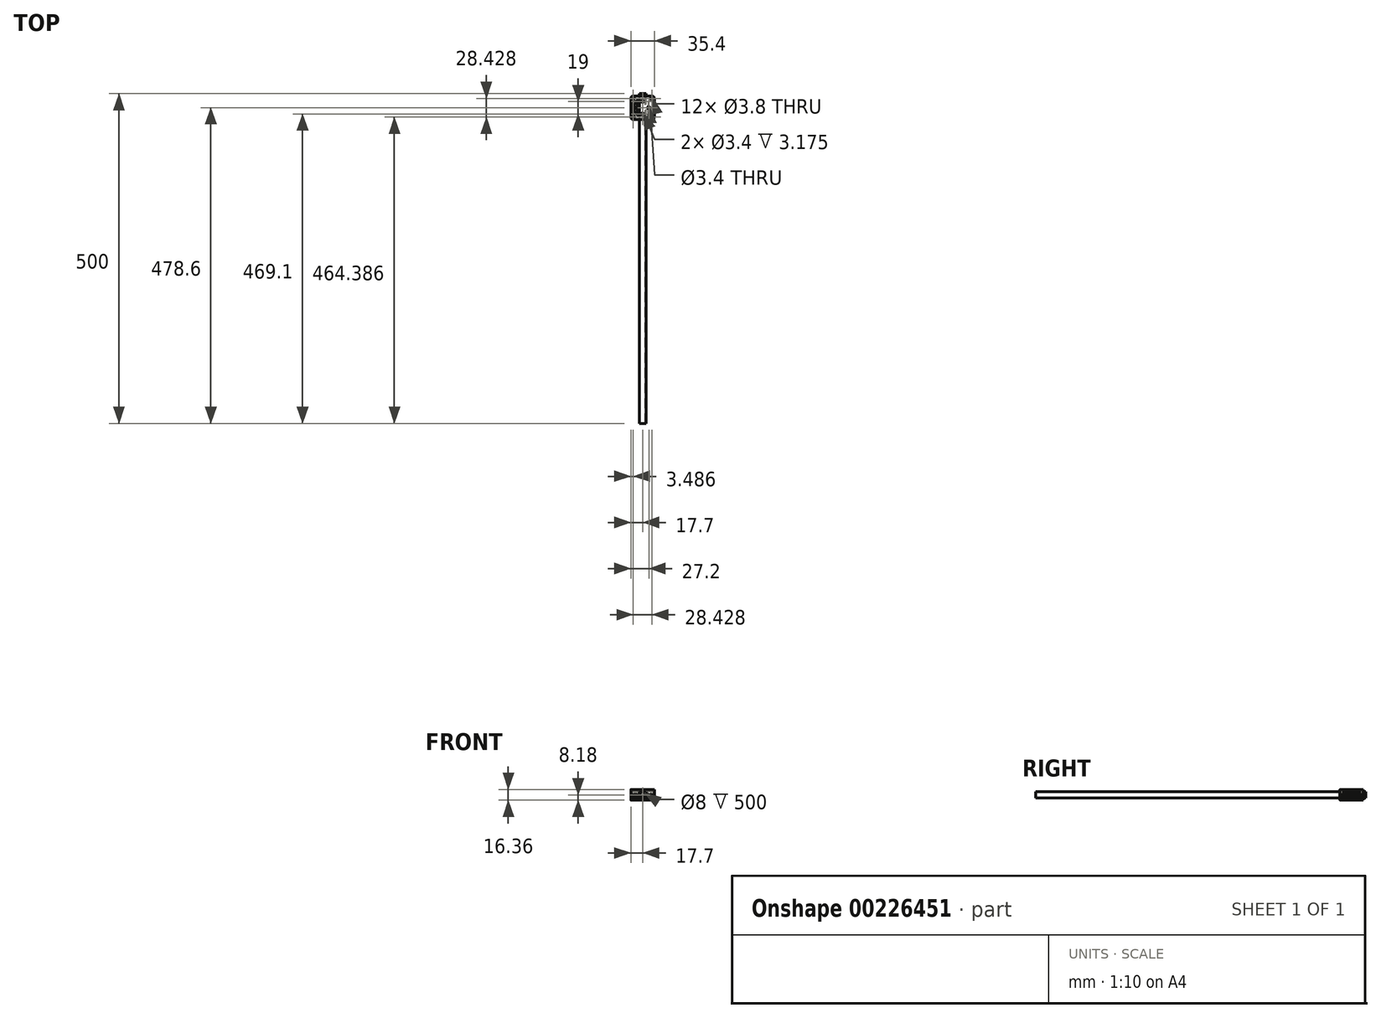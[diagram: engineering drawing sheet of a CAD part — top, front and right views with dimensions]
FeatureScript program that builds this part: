
annotation { "Feature Type Name" : "Feature", "Feature Type Description" : "" }
export const myFeature = defineFeature(function(context is Context, id is Id, definition is map)
    precondition{}
    {
        {
            var Q0;
            Q0=qCreatedBy(makeId("Front.planeOp"),FACE);
            var sketch = newSketch(context, id + "F0", { "sketchPlane" : qUnion([Q0])});
            skLineSegment(sketch, "E0.bottom", {"start": v(-5, 5) * mm, "end": v(5, 5) * mm});
            skLineSegment(sketch, "E0.top", {"start": v(-5, -5) * mm, "end": v(5, -5) * mm});
            skLineSegment(sketch, "E0.left", {"start": v(-5, 5) * mm, "end": v(-5, -5) * mm});
            skLineSegment(sketch, "E0.right", {"start": v(5, 5) * mm, "end": v(5, -5) * mm});
            skPoint(sketch, "E0.middle", {"position": v(0, 0) * mm});
            skCircle(sketch, "E1", {"center": v(0, 0) * mm, "radius": 4 * mm});
            skSolve(sketch);
        }
        {
            var Q0;
            Q0 = qSketchRegion(id + "F0", true);
            extrude(context, id + "F1", {"entities" : qUnion([Q0]), "depth" : 500 * mm, "offsetDistance" : 25.4 * mm, "symmetric" : true});
        }
        {
            var Q0;
            Q0=makeQuery(id+"F1.opExtrude","SWEPT_FACE",FACE,{"disambiguationData":[OSD([sQuery(id+"F0.wireOp",EDGE,"E0.bottom")])]});
            var sketch = newSketch(context, id + "F2", { "sketchPlane" : qUnion([Q0])});
            skCircle(sketch, "E2", {"center": v(0, 228.6) * mm, "radius": 13.5 * mm});
            skCircle(sketch, "E3", {"center": v(0, 228.6) * mm, "radius": 16.67 * mm});
            skLineSegment(sketch, "E4.bottom", {"start": v(-14.52, 246.3) * mm, "end": v(14.52, 246.3) * mm});
            skLineSegment(sketch, "E4.top", {"start": v(-14.52, 210.9) * mm, "end": v(14.52, 210.9) * mm});
            skLineSegment(sketch, "E4.left", {"start": v(-17.7, 243.12) * mm, "end": v(-17.7, 214.08) * mm});
            skLineSegment(sketch, "E4.right", {"start": v(17.7, 243.13) * mm, "end": v(17.7, 214.08) * mm});
            skLineSegment(sketch, "E5", {"start": v(-17.7, 210.9) * mm, "end": v(17.7, 246.3) * mm, "construction": true});
            skCircle(sketch, "E6", {"center": v(-14.21, 214.39) * mm, "radius": 1.9 * mm});
            skLineSegment(sketch, "E7", {"start": v(0, 228.6) * mm, "end": v(0, 246.3) * mm, "construction": true});
            skCircle(sketch, "E8.MirrorC", {"center": v(14.21, 214.39) * mm, "radius": 1.9 * mm});
            skLineSegment(sketch, "E9", {"start": v(0, 228.6) * mm, "end": v(17.7, 228.6) * mm, "construction": true});
            skCircle(sketch, "E10.MirrorC", {"center": v(14.21, 242.81) * mm, "radius": 1.9 * mm});
            skCircle(sketch, "E11.MirrorC", {"center": v(-14.21, 242.81) * mm, "radius": 1.9 * mm});
            skPoint(sketch, "E12.visualSharp", {"position": v(-17.7, 246.3) * mm});
            skArc(sketch, "E12.filletArc", {"start": v(-14.52, 246.3) * mm, "mid": v(-16.77, 245.37) * mm, "end": v(-17.7, 243.12) * mm});
            skPoint(sketch, "E13.visualSharp", {"position": v(17.7, 246.3) * mm});
            skArc(sketch, "E13.filletArc", {"start": v(17.7, 243.13) * mm, "mid": v(16.77, 245.37) * mm, "end": v(14.52, 246.3) * mm});
            skPoint(sketch, "E14.visualSharp", {"position": v(17.7, 210.9) * mm});
            skArc(sketch, "E14.filletArc", {"start": v(14.52, 210.9) * mm, "mid": v(16.77, 211.83) * mm, "end": v(17.7, 214.08) * mm});
            skPoint(sketch, "E15.visualSharp", {"position": v(-17.7, 210.9) * mm});
            skArc(sketch, "E15.filletArc", {"start": v(-17.7, 214.08) * mm, "mid": v(-16.77, 211.83) * mm, "end": v(-14.52, 210.9) * mm});
            skCircle(sketch, "E16", {"center": v(0, 219.1) * mm, "radius": 1.7 * mm});
            skCircle(sketch, "E17.MirrorC", {"center": v(0, 238.1) * mm, "radius": 1.7 * mm});
            skCircle(sketch, "E18.MirrorC", {"center": v(9.5, 228.6) * mm, "radius": 1.7 * mm});
            skCircle(sketch, "E19.MirrorC", {"center": v(-9.5, 228.6) * mm, "radius": 1.7 * mm});
            skSolve(sketch);
        }
        {
            var Q0;
            Q0=makeQuery(id+"F2.imprint","IMPRINT",FACE,{"disambiguationData":[TD([[makeQuery(id+"F2.imprint","IMPRINT",EDGE,{"derivedFrom":sQuery(id+"F2.wireOp",EDGE,"E4.left")}),1.0]])]});
            var Q1;
            {var subQ0=sQuery(id+"F2.wireOp",EDGE,"E3");var subQ1=sQuery(id+"F0.wireOp",EDGE,"E0.bottom");var subQ2=makeQuery(id+"F1.opExtrude","SWEPT_EDGE",EDGE,{"disambiguationData":[OSD([subQ1,sQuery(id+"F0.wireOp",EDGE,"E0.left")])]});var subQ3=makeQuery(id+"F2.imprint","INTERSECT",VERTEX,{"disambiguationData":[OD(0.0)],"derivedFrom":[subQ2,subQ0]});Q1=makeQuery(id+"F2.imprint","IMPRINT",FACE,{"disambiguationData":[TD([[makeQuery(id+"F2.imprint","IMPRINT",EDGE,{"disambiguationData":[TD([[subQ3,1.0]])],"derivedFrom":subQ0}),-1.0]])]});}
            var Q2;
            Q2=makeQuery(id+"F2.imprint","IMPRINT",FACE,{"disambiguationData":[TD([[makeQuery(id+"F2.imprint","IMPRINT",EDGE,{"derivedFrom":sQuery(id+"F2.wireOp",EDGE,"E4.right")}),-1.0]])]});
            var Q3;
            {var subQ0=sQuery(id+"F2.wireOp",EDGE,"E2");var subQ1=makeQuery(id+"F1.opExtrude","SWEPT_EDGE",EDGE,{"disambiguationData":[OSD([sQuery(id+"F0.wireOp",EDGE,"E0.bottom"),sQuery(id+"F0.wireOp",EDGE,"E0.right")])]});var subQ2=makeQuery(id+"F2.imprint","INTERSECT",VERTEX,{"disambiguationData":[OD(0.0)],"derivedFrom":[subQ1,subQ0]});Q3=makeQuery(id+"F2.imprint","IMPRINT",FACE,{"disambiguationData":[TD([[makeQuery(id+"F2.imprint","IMPRINT",EDGE,{"disambiguationData":[TD([[subQ2,1.0]])],"derivedFrom":subQ0}),-1.0]])]});}
            var Q4;
            {var subQ0=sQuery(id+"F2.wireOp",EDGE,"E2");var subQ1=sQuery(id+"F0.wireOp",EDGE,"E0.bottom");var subQ2=makeQuery(id+"F1.opExtrude","SWEPT_EDGE",EDGE,{"disambiguationData":[OSD([subQ1,sQuery(id+"F0.wireOp",EDGE,"E0.left")])]});var subQ3=makeQuery(id+"F2.imprint","INTERSECT",VERTEX,{"disambiguationData":[OD(0.0)],"derivedFrom":[subQ2,subQ0]});Q4=makeQuery(id+"F2.imprint","IMPRINT",FACE,{"disambiguationData":[TD([[makeQuery(id+"F2.imprint","IMPRINT",EDGE,{"disambiguationData":[TD([[subQ3,1.0]])],"derivedFrom":subQ0}),-1.0]])]});}
            var Q5;
            {var subQ0=sQuery(id+"F2.wireOp",EDGE,"E2");var subQ1=makeQuery(id+"F1.opExtrude","SWEPT_EDGE",EDGE,{"disambiguationData":[OSD([sQuery(id+"F0.wireOp",EDGE,"E0.bottom"),sQuery(id+"F0.wireOp",EDGE,"E0.left")])]});var subQ2=makeQuery(id+"F2.imprint","INTERSECT",VERTEX,{"disambiguationData":[OD(0.0)],"derivedFrom":[subQ1,subQ0]});Q5=makeQuery(id+"F2.imprint","IMPRINT",FACE,{"disambiguationData":[TD([[makeQuery(id+"F2.imprint","IMPRINT",EDGE,{"disambiguationData":[TD([[subQ2,-1.0]])],"derivedFrom":subQ0}),-1.0]])]});}
            var Q6;
            Q6=makeQuery(id+"F2.imprint","IMPRINT",FACE,{"disambiguationData":[TD([[makeQuery(id+"F2.imprint","IMPRINT",EDGE,{"derivedFrom":sQuery(id+"F2.wireOp",EDGE,"E19.MirrorC")}),1.0]])]});
            var Q7;
            Q7=makeQuery(id+"F2.imprint","IMPRINT",FACE,{"disambiguationData":[TD([[makeQuery(id+"F2.imprint","IMPRINT",EDGE,{"derivedFrom":sQuery(id+"F2.wireOp",EDGE,"E16")}),-1.0]])]});
            var Q8;
            Q8=makeQuery(id+"F2.imprint","IMPRINT",FACE,{"disambiguationData":[TD([[makeQuery(id+"F2.imprint","IMPRINT",EDGE,{"derivedFrom":sQuery(id+"F2.wireOp",EDGE,"E18.MirrorC")}),-1.0]])]});
            var Q9;
            {var subQ0=sQuery(id+"F2.wireOp",EDGE,"E2");var subQ1=sQuery(id+"F0.wireOp",EDGE,"E0.bottom");var subQ2=makeQuery(id+"F1.opExtrude","SWEPT_EDGE",EDGE,{"disambiguationData":[OSD([subQ1,sQuery(id+"F0.wireOp",EDGE,"E0.left")])]});var subQ3=makeQuery(id+"F2.imprint","INTERSECT",VERTEX,{"disambiguationData":[OD(1.0)],"derivedFrom":[subQ2,subQ0]});Q9=makeQuery(id+"F2.imprint","IMPRINT",FACE,{"disambiguationData":[TD([[makeQuery(id+"F2.imprint","IMPRINT",EDGE,{"disambiguationData":[TD([[subQ3,-1.0]])],"derivedFrom":subQ0}),-1.0]])]});}
            var Q10;
            {var subQ0=sQuery(id+"F2.wireOp",EDGE,"E3");var subQ1=sQuery(id+"F0.wireOp",EDGE,"E0.bottom");var subQ2=makeQuery(id+"F1.opExtrude","SWEPT_EDGE",EDGE,{"disambiguationData":[OSD([subQ1,sQuery(id+"F0.wireOp",EDGE,"E0.left")])]});var subQ3=makeQuery(id+"F2.imprint","INTERSECT",VERTEX,{"disambiguationData":[OD(1.0)],"derivedFrom":[subQ2,subQ0]});Q10=makeQuery(id+"F2.imprint","IMPRINT",FACE,{"disambiguationData":[TD([[makeQuery(id+"F2.imprint","IMPRINT",EDGE,{"disambiguationData":[TD([[subQ3,-1.0]])],"derivedFrom":subQ0}),-1.0]])]});}
            extrude(context, id + "F3", {"entities" : qUnion([Q0, Q1, Q2, Q3, Q4, Q5, Q6, Q7, Q8, Q9, Q10]), "depth" : 3.17 * mm, "offsetDistance" : 25.4 * mm});
        }
        {
            var Q0;
            Q0=makeQuery(id+"F3.opExtrude","CAP_FACE",FACE,{"disambiguationData":[OSD([sQuery(id+"F2.wireOp",EDGE,"E4.bottom"),sQuery(id+"F2.wireOp",EDGE,"E4.top"),sQuery(id+"F2.wireOp",EDGE,"E4.left"),sQuery(id+"F2.wireOp",EDGE,"E4.right"),sQuery(id+"F2.wireOp",EDGE,"E6"),sQuery(id+"F2.wireOp",EDGE,"E8.MirrorC"),sQuery(id+"F2.wireOp",EDGE,"E10.MirrorC"),sQuery(id+"F2.wireOp",EDGE,"E11.MirrorC"),sQuery(id+"F2.wireOp",EDGE,"E12.filletArc"),sQuery(id+"F2.wireOp",EDGE,"E13.filletArc"),sQuery(id+"F2.wireOp",EDGE,"E14.filletArc"),sQuery(id+"F2.wireOp",EDGE,"E15.filletArc"),sQuery(id+"F2.wireOp",EDGE,"E16"),sQuery(id+"F2.wireOp",EDGE,"E17.MirrorC"),sQuery(id+"F2.wireOp",EDGE,"E18.MirrorC"),sQuery(id+"F2.wireOp",EDGE,"E19.MirrorC")])],"isStart":true});
            var sketch = newSketch(context, id + "F4", { "sketchPlane" : qUnion([Q0])});
            skLineSegment(sketch, "E20", {"start": v(-14.52, -217.87) * mm, "end": v(-11.35, -217.87) * mm});
            skLineSegment(sketch, "E21", {"start": v(-8.18, -221.05) * mm, "end": v(-8.18, -225.63) * mm});
            skPoint(sketch, "E22", {"position": v(-9.5, -228.6) * mm});
            skPoint(sketch, "E23.orphan", {"position": v(-8.18, -228.6) * mm});
            skLineSegment(sketch, "E24", {"start": v(-9.5, -228.6) * mm, "end": v(9.5, -228.6) * mm, "construction": true});
            skLineSegment(sketch, "E25.MirrorCS", {"start": v(-8.18, -236.15) * mm, "end": v(-8.18, -231.57) * mm});
            skLineSegment(sketch, "E26.MirrorCS", {"start": v(-14.52, -239.33) * mm, "end": v(-11.35, -239.33) * mm});
            skPoint(sketch, "E27.visualSharp", {"position": v(-8.18, -217.87) * mm});
            skArc(sketch, "E27.filletArc", {"start": v(-8.18, -221.05) * mm, "mid": v(-9.1, -218.8) * mm, "end": v(-11.35, -217.87) * mm});
            skPoint(sketch, "E28.visualSharp", {"position": v(-8.18, -239.33) * mm});
            skArc(sketch, "E28.filletArc", {"start": v(-11.35, -239.33) * mm, "mid": v(-9.1, -238.4) * mm, "end": v(-8.17, -236.15) * mm});
            skLineSegment(sketch, "E29.0", {"start": v(-17.7, -214.7) * mm, "end": v(-17.7, -214.08) * mm});
            skArc(sketch, "E29.1", {"start": v(-17.7, -214.08) * mm, "mid": v(-16.77, -211.83) * mm, "end": v(-14.52, -210.9) * mm});
            skLineSegment(sketch, "E29.2", {"start": v(-14.52, -210.9) * mm, "end": v(14.52, -210.9) * mm});
            skArc(sketch, "E29.3", {"start": v(14.52, -210.9) * mm, "mid": v(16.77, -211.83) * mm, "end": v(17.7, -214.08) * mm});
            skLineSegment(sketch, "E29.4", {"start": v(17.7, -243.13) * mm, "end": v(17.7, -214.08) * mm});
            skLineSegment(sketch, "E29.5", {"start": v(-14.52, -246.3) * mm, "end": v(14.52, -246.3) * mm});
            skArc(sketch, "E29.6", {"start": v(-14.52, -246.3) * mm, "mid": v(-16.77, -245.37) * mm, "end": v(-17.7, -243.12) * mm});
            skArc(sketch, "E29.7", {"start": v(17.7, -243.13) * mm, "mid": v(16.77, -245.37) * mm, "end": v(14.52, -246.3) * mm});
            skLineSegment(sketch, "E30", {"start": v(0, -246.3) * mm, "end": v(0, -210.9) * mm, "construction": true});
            skPoint(sketch, "E31.newPointA", {"position": v(-17.7, -243.12) * mm});
            skPoint(sketch, "E31.newPointB", {"position": v(-17.7, -217.87) * mm});
            skArc(sketch, "E31.filletArc", {"start": v(-17.7, -214.7) * mm, "mid": v(-16.77, -216.94) * mm, "end": v(-14.52, -217.87) * mm});
            skLineSegment(sketch, "E32", {"start": v(-17.7, -242.5) * mm, "end": v(-17.7, -243.12) * mm});
            skPoint(sketch, "E33.visualSharp", {"position": v(-17.7, -239.33) * mm});
            skArc(sketch, "E33.filletArc", {"start": v(-14.52, -239.33) * mm, "mid": v(-16.77, -240.26) * mm, "end": v(-17.7, -242.5) * mm});
            skArc(sketch, "E34.MirrorCS", {"start": v(17.7, -214.7) * mm, "mid": v(16.77, -216.94) * mm, "end": v(14.52, -217.87) * mm});
            skLineSegment(sketch, "E35.MirrorCS", {"start": v(14.52, -217.87) * mm, "end": v(11.35, -217.87) * mm});
            skArc(sketch, "E36.MirrorCS", {"start": v(8.18, -221.05) * mm, "mid": v(9.1, -218.8) * mm, "end": v(11.35, -217.87) * mm});
            skLineSegment(sketch, "E37.MirrorCS", {"start": v(8.18, -221.05) * mm, "end": v(8.18, -225.63) * mm});
            skLineSegment(sketch, "E38.MirrorCS", {"start": v(8.17, -236.15) * mm, "end": v(8.17, -231.57) * mm});
            skArc(sketch, "E39.MirrorCS", {"start": v(11.35, -239.33) * mm, "mid": v(9.1, -238.4) * mm, "end": v(8.17, -236.15) * mm});
            skLineSegment(sketch, "E40.MirrorCS", {"start": v(14.52, -239.33) * mm, "end": v(11.35, -239.33) * mm});
            skArc(sketch, "E41.MirrorCS", {"start": v(14.52, -239.33) * mm, "mid": v(16.77, -240.26) * mm, "end": v(17.7, -242.5) * mm});
            skLineSegment(sketch, "E42.0", {"start": v(-5, 250) * mm, "end": v(-5, -250) * mm});
            skLineSegment(sketch, "E43.0", {"start": v(5, 250) * mm, "end": v(5, -250) * mm});
            skArc(sketch, "E44", {"start": v(-8.18, -231.57) * mm, "mid": v(-6.25, -228.6) * mm, "end": v(-8.18, -225.63) * mm});
            skArc(sketch, "E45.MirrorC", {"start": v(8.18, -231.57) * mm, "mid": v(6.25, -228.6) * mm, "end": v(8.18, -225.63) * mm});
            skSolve(sketch);
        }
        {
            var Q0;
            Q0=makeQuery(id+"F4.imprint","IMPRINT",FACE,{"disambiguationData":[TD([[makeQuery(id+"F4.imprint","IMPRINT",EDGE,{"derivedFrom":sQuery(id+"F4.wireOp",EDGE,"E20")}),1.0]])]});
            var Q1;
            {var subQ4=sQuery(id+"F4.wireOp",EDGE,"E29.3");Q1=makeQuery(id+"F4.imprint","IMPRINT",FACE,{"disambiguationData":[TD([[makeQuery(id+"F4.imprint","IMPRINT",EDGE,{"derivedFrom":subQ4}),-1.0]])]});}
            extrude(context, id + "F5", {"entities" : qUnion([Q0, Q1]), "operationType" : NewBodyOperationType.ADD, "depth" : 4.5 * mm, "offsetDistance" : 25.4 * mm});
        }
        {
            var Q0;
            Q0=makeQuery(id+"F5.opExtrude","CAP_FACE",FACE,{"disambiguationData":[OSD([sQuery(id+"F2.wireOp",EDGE,"E6"),sQuery(id+"F2.wireOp",EDGE,"E11.MirrorC"),sQuery(id+"F4.wireOp",EDGE,"E20"),sQuery(id+"F4.wireOp",EDGE,"E21"),sQuery(id+"F4.wireOp",EDGE,"86f816a6-afa7-4e7c-9506-ce16fb6d2d9a.0"),sQuery(id+"F4.wireOp",EDGE,"E25.MirrorCS"),sQuery(id+"F4.wireOp",EDGE,"E26.MirrorCS"),sQuery(id+"F4.wireOp",EDGE,"E27.filletArc"),sQuery(id+"F4.wireOp",EDGE,"E28.filletArc"),sQuery(id+"F4.wireOp",EDGE,"E29.0"),sQuery(id+"F4.wireOp",EDGE,"E29.1"),sQuery(id+"F4.wireOp",EDGE,"E29.2"),sQuery(id+"F4.wireOp",EDGE,"E29.5"),sQuery(id+"F4.wireOp",EDGE,"E29.6"),sQuery(id+"F4.wireOp",EDGE,"E31.filletArc"),sQuery(id+"F4.wireOp",EDGE,"E32"),sQuery(id+"F4.wireOp",EDGE,"E33.filletArc"),sQuery(id+"F4.wireOp",EDGE,"E42.0")])],"isStart":false});
            cPlane(context, id + "F6", {"entities" : qUnion([Q0]), "cplaneType" : CPlaneType.OFFSET, "offset" : 1 * mm, "width" : 152.4 * mm, "height" : 152.4 * mm});
        }
        {
            var Q0;
            Q0=qCreatedBy(id+"F6.planeOp",FACE);
            var sketch = newSketch(context, id + "F7", { "sketchPlane" : qUnion([Q0])});
            skLineSegment(sketch, "E46.0", {"start": v(-14.52, -210.9) * mm, "end": v(-5, -210.9) * mm});
            skArc(sketch, "E46.1", {"start": v(-17.7, -214.08) * mm, "mid": v(-16.77, -211.83) * mm, "end": v(-14.52, -210.9) * mm});
            skArc(sketch, "E46.2", {"start": v(-17.7, -214.7) * mm, "mid": v(-16.77, -216.94) * mm, "end": v(-14.52, -217.87) * mm});
            skLineSegment(sketch, "E46.3", {"start": v(-17.7, -214.7) * mm, "end": v(-17.7, -214.08) * mm});
            skCircle(sketch, "E46.4", {"center": v(-14.21, -214.39) * mm, "radius": 1.9 * mm});
            skLineSegment(sketch, "E46.5", {"start": v(-14.52, -217.87) * mm, "end": v(-11.35, -217.87) * mm});
            skArc(sketch, "E46.6", {"start": v(-8.18, -221.05) * mm, "mid": v(-9.1, -218.8) * mm, "end": v(-11.35, -217.87) * mm});
            skLineSegment(sketch, "E46.9", {"start": v(-8.18, -236.15) * mm, "end": v(-8.18, -231.57) * mm});
            skArc(sketch, "E46.10", {"start": v(-11.35, -239.33) * mm, "mid": v(-9.1, -238.4) * mm, "end": v(-8.17, -236.15) * mm});
            skLineSegment(sketch, "E46.11", {"start": v(-14.52, -239.33) * mm, "end": v(-11.35, -239.33) * mm});
            skArc(sketch, "E46.12", {"start": v(-14.52, -239.33) * mm, "mid": v(-16.77, -240.26) * mm, "end": v(-17.7, -242.5) * mm});
            skLineSegment(sketch, "E46.13", {"start": v(-17.7, -243.12) * mm, "end": v(-17.7, -242.5) * mm});
            skArc(sketch, "E46.14", {"start": v(-14.52, -246.3) * mm, "mid": v(-16.77, -245.37) * mm, "end": v(-17.7, -243.12) * mm});
            skLineSegment(sketch, "E46.15", {"start": v(-14.52, -246.3) * mm, "end": v(-5, -246.3) * mm});
            skLineSegment(sketch, "E46.16", {"start": v(5, -246.3) * mm, "end": v(14.52, -246.3) * mm});
            skArc(sketch, "E46.17", {"start": v(17.7, -243.13) * mm, "mid": v(16.77, -245.37) * mm, "end": v(14.52, -246.3) * mm});
            skLineSegment(sketch, "E46.18", {"start": v(17.7, -243.13) * mm, "end": v(17.7, -242.5) * mm});
            skArc(sketch, "E46.19", {"start": v(14.52, -239.33) * mm, "mid": v(16.77, -240.26) * mm, "end": v(17.7, -242.5) * mm});
            skLineSegment(sketch, "E46.20", {"start": v(14.52, -239.33) * mm, "end": v(11.35, -239.33) * mm});
            skArc(sketch, "E46.21", {"start": v(11.35, -239.33) * mm, "mid": v(9.1, -238.4) * mm, "end": v(8.17, -236.15) * mm});
            skCircle(sketch, "E46.22", {"center": v(14.21, -242.81) * mm, "radius": 1.9 * mm});
            skCircle(sketch, "E46.23", {"center": v(-14.21, -242.81) * mm, "radius": 1.9 * mm});
            skLineSegment(sketch, "E46.26", {"start": v(8.18, -221.05) * mm, "end": v(8.18, -225.63) * mm});
            skArc(sketch, "E46.27", {"start": v(8.18, -221.05) * mm, "mid": v(9.1, -218.8) * mm, "end": v(11.35, -217.87) * mm});
            skLineSegment(sketch, "E46.28", {"start": v(14.52, -217.87) * mm, "end": v(11.35, -217.87) * mm});
            skArc(sketch, "E46.29", {"start": v(17.7, -214.7) * mm, "mid": v(16.77, -216.94) * mm, "end": v(14.52, -217.87) * mm});
            skLineSegment(sketch, "E46.30", {"start": v(17.7, -214.7) * mm, "end": v(17.7, -214.08) * mm});
            skArc(sketch, "E46.31", {"start": v(14.52, -210.9) * mm, "mid": v(16.77, -211.83) * mm, "end": v(17.7, -214.08) * mm});
            skCircle(sketch, "E46.32", {"center": v(14.21, -214.39) * mm, "radius": 1.9 * mm});
            skLineSegment(sketch, "E46.33", {"start": v(5, -210.9) * mm, "end": v(14.52, -210.9) * mm});
            skLineSegment(sketch, "E46.34", {"start": v(5, 250) * mm, "end": v(5, -250) * mm});
            skLineSegment(sketch, "E46.35", {"start": v(-5, 250) * mm, "end": v(-5, -250) * mm});
            skLineSegment(sketch, "E47.0", {"start": v(-8.18, -221.05) * mm, "end": v(-8.18, -225.63) * mm});
            skArc(sketch, "E47.1", {"start": v(-8.18, -231.57) * mm, "mid": v(-6.25, -228.6) * mm, "end": v(-8.18, -225.63) * mm});
            skLineSegment(sketch, "E48.0", {"start": v(8.17, -236.15) * mm, "end": v(8.17, -231.57) * mm});
            skArc(sketch, "E48.1", {"start": v(8.18, -231.57) * mm, "mid": v(6.25, -228.6) * mm, "end": v(8.18, -225.63) * mm});
            skSolve(sketch);
        }
        {
            var Q0;
            Q0 = qSketchRegion(id + "F7", true);
            extrude(context, id + "F8", {"entities" : qUnion([Q0]), "depth" : 4.5 * mm, "offsetDistance" : 25.4 * mm});
        }
        {
            var Q0;
            Q0=makeQuery(id+"F8.opExtrude","CAP_FACE",FACE,{"disambiguationData":[OSD([sQuery(id+"F7.wireOp",EDGE,"E46.0"),sQuery(id+"F7.wireOp",EDGE,"E46.1"),sQuery(id+"F7.wireOp",EDGE,"E46.2"),sQuery(id+"F7.wireOp",EDGE,"E46.3"),sQuery(id+"F7.wireOp",EDGE,"E46.4"),sQuery(id+"F7.wireOp",EDGE,"E46.5"),sQuery(id+"F7.wireOp",EDGE,"E46.6"),sQuery(id+"F7.wireOp",EDGE,"E46.7"),sQuery(id+"F7.wireOp",EDGE,"E46.8"),sQuery(id+"F7.wireOp",EDGE,"E46.9"),sQuery(id+"F7.wireOp",EDGE,"E46.10"),sQuery(id+"F7.wireOp",EDGE,"E46.11"),sQuery(id+"F7.wireOp",EDGE,"E46.12"),sQuery(id+"F7.wireOp",EDGE,"E46.13"),sQuery(id+"F7.wireOp",EDGE,"E46.14"),sQuery(id+"F7.wireOp",EDGE,"E46.15"),sQuery(id+"F7.wireOp",EDGE,"E46.23"),sQuery(id+"F7.wireOp",EDGE,"E46.35")])],"isStart":false});
            var sketch = newSketch(context, id + "F9", { "sketchPlane" : qUnion([Q0])});
            skLineSegment(sketch, "E49", {"start": v(-5, -246.3) * mm, "end": v(5, -246.3) * mm});
            skLineSegment(sketch, "E50", {"start": v(-5, -210.9) * mm, "end": v(5, -210.9) * mm});
            skLineSegment(sketch, "E51.0", {"start": v(5, -246.3) * mm, "end": v(14.52, -246.3) * mm});
            skArc(sketch, "E51.1", {"start": v(17.7, -243.13) * mm, "mid": v(16.77, -245.37) * mm, "end": v(14.52, -246.3) * mm});
            skLineSegment(sketch, "E51.2", {"start": v(17.7, -243.13) * mm, "end": v(17.7, -242.5) * mm});
            skArc(sketch, "E51.3", {"start": v(14.52, -239.33) * mm, "mid": v(16.77, -240.26) * mm, "end": v(17.7, -242.5) * mm});
            skLineSegment(sketch, "E51.4", {"start": v(14.52, -239.33) * mm, "end": v(11.35, -239.33) * mm});
            skArc(sketch, "E51.7", {"start": v(8.18, -231.57) * mm, "mid": v(6.25, -228.6) * mm, "end": v(8.18, -225.63) * mm});
            skLineSegment(sketch, "E51.8", {"start": v(8.18, -221.05) * mm, "end": v(8.18, -225.63) * mm});
            skArc(sketch, "E51.9", {"start": v(8.17, -221.05) * mm, "mid": v(9.1, -218.8) * mm, "end": v(11.35, -217.87) * mm});
            skLineSegment(sketch, "E51.10", {"start": v(14.52, -217.87) * mm, "end": v(11.35, -217.87) * mm});
            skArc(sketch, "E51.11", {"start": v(17.7, -214.7) * mm, "mid": v(16.77, -216.94) * mm, "end": v(14.52, -217.87) * mm});
            skLineSegment(sketch, "E51.12", {"start": v(17.7, -214.7) * mm, "end": v(17.7, -214.08) * mm});
            skArc(sketch, "E51.13", {"start": v(14.52, -210.9) * mm, "mid": v(16.77, -211.83) * mm, "end": v(17.7, -214.08) * mm});
            skLineSegment(sketch, "E51.14", {"start": v(5, -210.9) * mm, "end": v(14.52, -210.9) * mm});
            skLineSegment(sketch, "E52", {"start": v(0, -210.9) * mm, "end": v(0, -246.3) * mm, "construction": true});
            skLineSegment(sketch, "E53.MirrorCS", {"start": v(-17.7, -214.7) * mm, "end": v(-17.7, -214.08) * mm});
            skLineSegment(sketch, "E54.MirrorCS", {"start": v(-17.7, -243.13) * mm, "end": v(-17.7, -242.5) * mm});
            skLineSegment(sketch, "E55.MirrorCS", {"start": v(-14.52, -239.33) * mm, "end": v(-11.35, -239.33) * mm});
            skArc(sketch, "E56.MirrorCS", {"start": v(-8.18, -231.57) * mm, "mid": v(-6.25, -228.6) * mm, "end": v(-8.18, -225.63) * mm});
            skLineSegment(sketch, "E57.MirrorCS", {"start": v(-14.52, -217.87) * mm, "end": v(-11.35, -217.87) * mm});
            skArc(sketch, "E58.MirrorCS", {"start": v(-17.7, -214.7) * mm, "mid": v(-16.77, -216.94) * mm, "end": v(-14.52, -217.87) * mm});
            skArc(sketch, "E59.MirrorCS", {"start": v(-14.52, -210.9) * mm, "mid": v(-16.77, -211.83) * mm, "end": v(-17.7, -214.08) * mm});
            skLineSegment(sketch, "E60.MirrorCS", {"start": v(-5, -246.3) * mm, "end": v(-14.52, -246.3) * mm});
            skArc(sketch, "E61.MirrorCS", {"start": v(-17.7, -243.13) * mm, "mid": v(-16.77, -245.37) * mm, "end": v(-14.52, -246.3) * mm});
            skLineSegment(sketch, "E62.MirrorCS", {"start": v(-5, -210.9) * mm, "end": v(-14.52, -210.9) * mm});
            skArc(sketch, "E63.MirrorCS", {"start": v(-14.52, -239.33) * mm, "mid": v(-16.77, -240.26) * mm, "end": v(-17.7, -242.5) * mm});
            skLineSegment(sketch, "E64.MirrorCS", {"start": v(-8.18, -221.05) * mm, "end": v(-8.18, -225.63) * mm});
            skArc(sketch, "E65.MirrorCS", {"start": v(-8.18, -221.05) * mm, "mid": v(-9.1, -218.8) * mm, "end": v(-11.35, -217.87) * mm});
            skCircle(sketch, "E66.0", {"center": v(-14.21, -214.39) * mm, "radius": 1.9 * mm});
            skCircle(sketch, "E67.0", {"center": v(14.21, -214.39) * mm, "radius": 1.9 * mm});
            skCircle(sketch, "E68.0", {"center": v(14.21, -242.81) * mm, "radius": 1.9 * mm});
            skCircle(sketch, "E69.0", {"center": v(-14.21, -242.81) * mm, "radius": 1.9 * mm});
            skLineSegment(sketch, "E70.0", {"start": v(8.17, -236.15) * mm, "end": v(8.17, -231.57) * mm});
            skArc(sketch, "E71.0", {"start": v(11.35, -239.33) * mm, "mid": v(9.1, -238.4) * mm, "end": v(8.17, -236.15) * mm});
            skLineSegment(sketch, "E72.0", {"start": v(-8.18, -236.15) * mm, "end": v(-8.18, -231.57) * mm});
            skArc(sketch, "E72.1", {"start": v(-11.35, -239.33) * mm, "mid": v(-9.1, -238.4) * mm, "end": v(-8.17, -236.15) * mm});
            skSolve(sketch);
        }
        {
            var Q0;
            Q0=makeQuery(id+"F9.imprint","IMPRINT",FACE,{"disambiguationData":[TD([[makeQuery(id+"F9.imprint","IMPRINT",EDGE,{"derivedFrom":sQuery(id+"F9.wireOp",EDGE,"E49")}),1.0]])]});
            var Q1;
            Q1=makeQuery(id+"F9.imprint","IMPRINT",FACE,{"disambiguationData":[TD([[makeQuery(id+"F9.imprint","IMPRINT",EDGE,{"derivedFrom":sQuery(id+"F9.wireOp",EDGE,"E53.MirrorCS")}),-1.0]])]});
            extrude(context, id + "F10", {"entities" : qUnion([Q0, Q1]), "depth" : 3.17 * mm, "offsetDistance" : 25.4 * mm});
        }
    });
